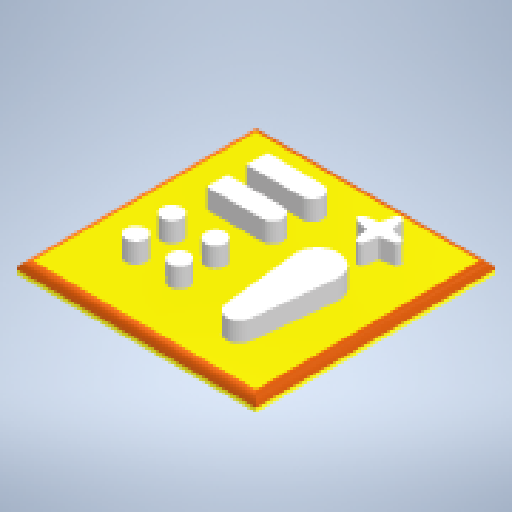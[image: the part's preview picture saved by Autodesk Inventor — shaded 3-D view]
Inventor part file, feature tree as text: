
AUTODESK INVENTOR PART (.ipt)
format: ipt  version: 2025.2 (Build 292293000, 293)  size: 316,416 bytes
history: native  units: mm
features: sketch x3, extrude x2, other x1, fillet x1
ambient origin geometry x8: Origin, YZ Plane, XZ Plane, XY Plane, X Axis, Y Axis, Z Axis, Center Point
bodies: Body1 (feature_tree)
feature tree (7):
  other  "Sólido1"
  extrude  "Extrusión1"  Depth=600.0mm
  fillet  "Empalme1"  Radius=30.0mm
  extrude  "Extrusión2"  Depth=50.0mm
  sketch  "Boceto1"  dims[d0=600.0mm d1=600.0mm d2=30.0mm d3=0.0mm]
  sketch  "Boceto2"  dims[d6=50.0mm d7=50.0mm d8=50.0mm d9=40.0mm d11=360.0deg d13=50.0mm d14=0.0mm]
  sketch  "Boceto - Patrón circular1"  dims[d4=20.0mm d5=50.0mm]
